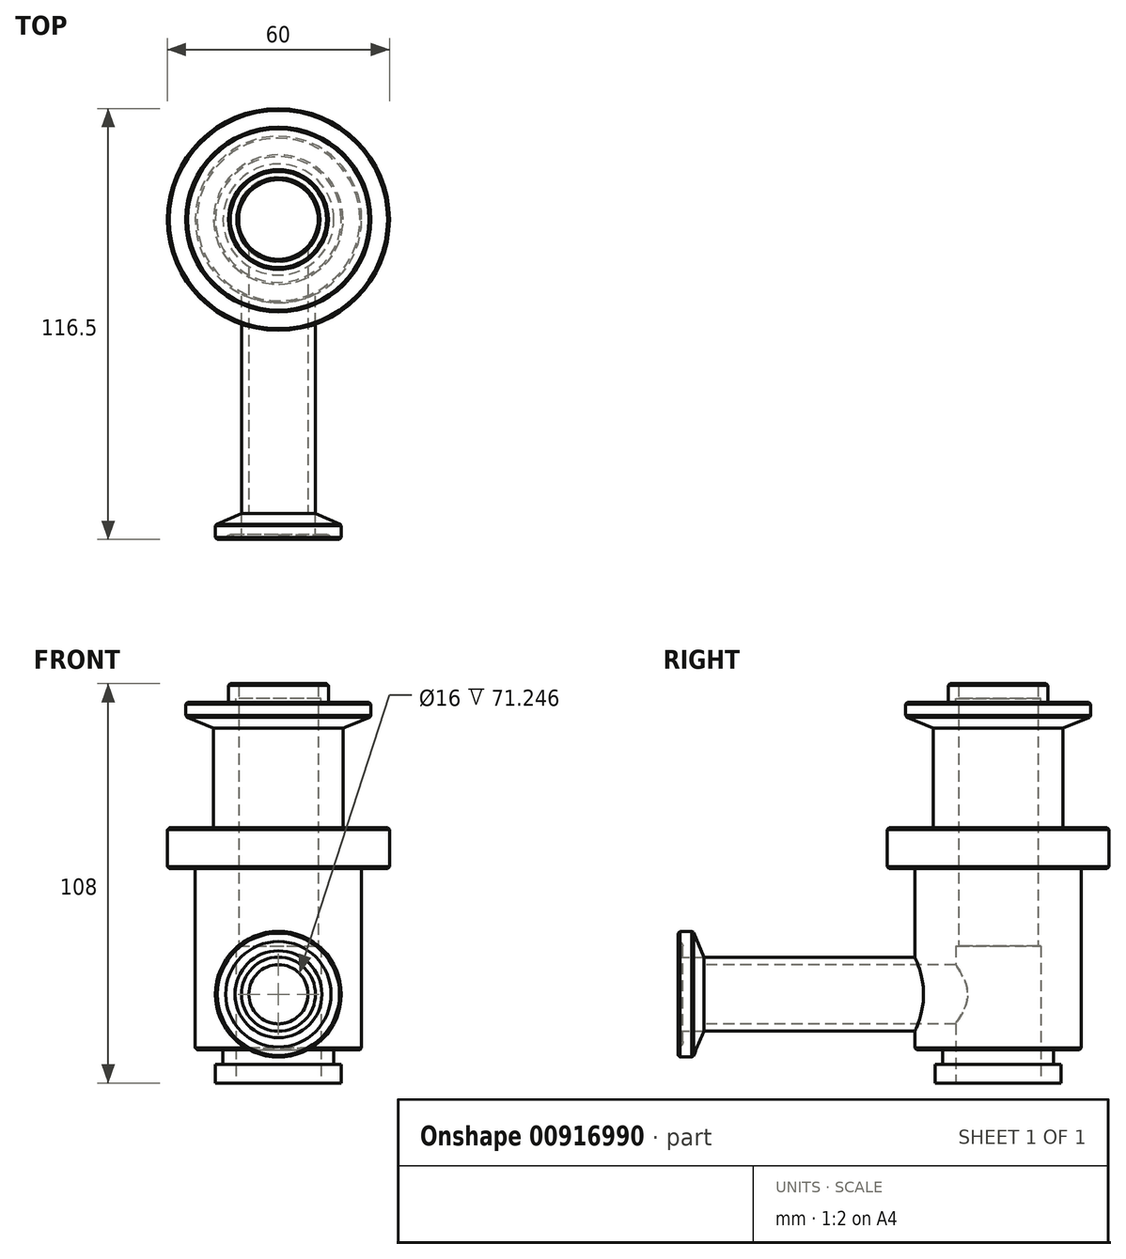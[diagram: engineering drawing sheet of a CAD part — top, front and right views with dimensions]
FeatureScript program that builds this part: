
annotation { "Feature Type Name" : "Feature", "Feature Type Description" : "" }
export const myFeature = defineFeature(function(context is Context, id is Id, definition is map)
    precondition{}
    {
        {
            var Q0;
            Q0=qCreatedBy(makeId("Top.planeOp"),FACE);
            var sketch = newSketch(context, id + "F0", { "sketchPlane" : qUnion([Q0])});
            skCircle(sketch, "E0", {"center": v(0, 0) * mm, "radius": 13.5 * mm});
            skCircle(sketch, "E1", {"center": v(0, 0) * mm, "radius": 10.75 * mm});
            skSolve(sketch);
        }
        {
            var Q0;
            Q0=makeQuery(id+"F0.imprint","IMPRINT",FACE,{"disambiguationData":[TD([[makeQuery(id+"F0.imprint","IMPRINT",EDGE,{"derivedFrom":sQuery(id+"F0.wireOp",EDGE,"E0")}),1.0]])]});
            extrude(context, id + "F1", {"entities" : qUnion([Q0]), "depth" : 5 * mm, "offsetDistance" : 25 * mm});
        }
        {
            var Q0;
            Q0=makeQuery(id+"F1.opExtrude","CAP_FACE",FACE,{"disambiguationData":[OSD([sQuery(id+"F0.wireOp",EDGE,"E0"),sQuery(id+"F0.wireOp",EDGE,"E1")])],"isStart":true});
            var sketch = newSketch(context, id + "F2", { "sketchPlane" : qUnion([Q0])});
            skCircle(sketch, "E2", {"center": v(0, 0) * mm, "radius": 25 * mm});
            skSolve(sketch);
        }
        {
            var Q0;
            Q0=makeQuery(id+"F2.imprint","IMPRINT",FACE,{"disambiguationData":[TD([[makeQuery(id+"F2.imprint","IMPRINT",EDGE,{"derivedFrom":makeQuery(id+"F1.opExtrude","CAP_EDGE",EDGE,{"disambiguationData":[OSD([sQuery(id+"F0.wireOp",EDGE,"E0")])],"isStart":true})}),-1.0]])]});
            var Q1;
            Q1=makeQuery(id+"F2.imprint","IMPRINT",FACE,{"disambiguationData":[TD([[makeQuery(id+"F2.imprint","IMPRINT",EDGE,{"derivedFrom":makeQuery(id+"F1.opExtrude","CAP_EDGE",EDGE,{"disambiguationData":[OSD([sQuery(id+"F0.wireOp",EDGE,"E1")])],"isStart":true})}),-1.0]])]});
            var Q2;
            Q2=makeQuery(id+"F2.imprint","IMPRINT",FACE,{"disambiguationData":[TD([[makeQuery(id+"F2.imprint","IMPRINT",EDGE,{"derivedFrom":sQuery(id+"F2.wireOp",EDGE,"E2")}),1.0]])]});
            extrude(context, id + "F3", {"entities" : qUnion([Q0, Q1, Q2]), "operationType" : NewBodyOperationType.ADD, "depth" : 7 * mm, "offsetDistance" : 25 * mm});
        }
        {
            var Q0;
            Q0=makeQuery(id+"F3.opExtrude","CAP_FACE",FACE,{"disambiguationData":[OSD([sQuery(id+"F2.wireOp",EDGE,"E2")])],"isStart":false});
            var sketch = newSketch(context, id + "F4", { "sketchPlane" : qUnion([Q0])});
            skCircle(sketch, "E3", {"center": v(0, 0) * mm, "radius": 17.5 * mm});
            skSolve(sketch);
        }
        {
            var Q0;
            Q0 = qSketchRegion(id + "F4", true);
            extrude(context, id + "F5", {"entities" : qUnion([Q0]), "operationType" : NewBodyOperationType.ADD, "depth" : 27 * mm, "offsetDistance" : 25 * mm});
        }
        {
            var Q0;
            Q0=makeQuery(id+"F5.opExtrude","CAP_FACE",FACE,{"disambiguationData":[OSD([sQuery(id+"F4.wireOp",EDGE,"E3")])],"isStart":false});
            var sketch = newSketch(context, id + "F6", { "sketchPlane" : qUnion([Q0])});
            skCircle(sketch, "E4", {"center": v(0, 0) * mm, "radius": 30 * mm});
            skSolve(sketch);
        }
        {
            var Q0;
            Q0=makeQuery(id+"F6.imprint","IMPRINT",FACE,{"disambiguationData":[TD([[makeQuery(id+"F6.imprint","IMPRINT",EDGE,{"derivedFrom":makeQuery(id+"F5.opExtrude","CAP_EDGE",EDGE,{"disambiguationData":[OSD([sQuery(id+"F4.wireOp",EDGE,"E3")])],"isStart":false})}),1.0]])]});
            var Q1;
            Q1=makeQuery(id+"F6.imprint","IMPRINT",FACE,{"disambiguationData":[TD([[makeQuery(id+"F6.imprint","IMPRINT",EDGE,{"derivedFrom":sQuery(id+"F6.wireOp",EDGE,"E4")}),1.0]])]});
            extrude(context, id + "F7", {"entities" : qUnion([Q0, Q1]), "operationType" : NewBodyOperationType.ADD, "depth" : 11 * mm, "offsetDistance" : 25 * mm});
        }
        {
            var Q0;
            Q0=makeQuery(id+"F7.opExtrude","CAP_FACE",FACE,{"disambiguationData":[OSD([sQuery(id+"F6.wireOp",EDGE,"E4")])],"isStart":false});
            var sketch = newSketch(context, id + "F8", { "sketchPlane" : qUnion([Q0])});
            skCircle(sketch, "E5", {"center": v(0, 0) * mm, "radius": 22.5 * mm});
            skSolve(sketch);
        }
        {
            var Q0;
            Q0=makeQuery(id+"F8.imprint","IMPRINT",FACE,{"disambiguationData":[TD([[makeQuery(id+"F8.imprint","IMPRINT",EDGE,{"derivedFrom":sQuery(id+"F8.wireOp",EDGE,"E5")}),1.0]])]});
            extrude(context, id + "F9", {"entities" : qUnion([Q0]), "operationType" : NewBodyOperationType.ADD, "depth" : 49 * mm, "offsetDistance" : 25 * mm});
        }
        {
            var Q0;
            Q0=makeQuery(id+"F9.opExtrude","CAP_FACE",FACE,{"disambiguationData":[OSD([sQuery(id+"F8.wireOp",EDGE,"E5")])],"isStart":false});
            var sketch = newSketch(context, id + "F10", { "sketchPlane" : qUnion([Q0])});
            skCircle(sketch, "E6", {"center": v(0, 0) * mm, "radius": 15 * mm});
            skSolve(sketch);
        }
        {
            var Q0;
            Q0=makeQuery(id+"F10.imprint","IMPRINT",FACE,{"disambiguationData":[TD([[makeQuery(id+"F10.imprint","IMPRINT",EDGE,{"derivedFrom":sQuery(id+"F10.wireOp",EDGE,"E6")}),1.0]])]});
            extrude(context, id + "F11", {"entities" : qUnion([Q0]), "operationType" : NewBodyOperationType.ADD, "depth" : 4 * mm, "offsetDistance" : 25 * mm});
        }
        {
            var Q0;
            Q0=makeQuery(id+"F11.opExtrude","CAP_FACE",FACE,{"disambiguationData":[OSD([sQuery(id+"F10.wireOp",EDGE,"E6")])],"isStart":false});
            var sketch = newSketch(context, id + "F12", { "sketchPlane" : qUnion([Q0])});
            skCircle(sketch, "E7", {"center": v(0, 0) * mm, "radius": 17 * mm});
            skSolve(sketch);
        }
        {
            var Q0;
            Q0=makeQuery(id+"F12.imprint","IMPRINT",FACE,{"disambiguationData":[TD([[makeQuery(id+"F12.imprint","IMPRINT",EDGE,{"derivedFrom":sQuery(id+"F12.wireOp",EDGE,"E7")}),1.0]])]});
            var Q1;
            Q1=makeQuery(id+"F12.imprint","IMPRINT",FACE,{"disambiguationData":[TD([[makeQuery(id+"F12.imprint","IMPRINT",EDGE,{"derivedFrom":makeQuery(id+"F11.opExtrude","CAP_EDGE",EDGE,{"disambiguationData":[OSD([sQuery(id+"F10.wireOp",EDGE,"E6")])],"isStart":false})}),1.0]])]});
            extrude(context, id + "F13", {"entities" : qUnion([Q0, Q1]), "operationType" : NewBodyOperationType.ADD, "depth" : 5 * mm, "offsetDistance" : 25 * mm});
        }
        {
            var Q0;
            Q0=makeQuery(id+"F13.opExtrude","CAP_FACE",FACE,{"disambiguationData":[OSD([sQuery(id+"F12.wireOp",EDGE,"E7")])],"isStart":false});
            var sketch = newSketch(context, id + "F14", { "sketchPlane" : qUnion([Q0])});
            skCircle(sketch, "E8", {"center": v(0, 0) * mm, "radius": 11.5 * mm});
            skSolve(sketch);
        }
        {
            var Q0;
            Q0=makeQuery(id+"F14.imprint","IMPRINT",FACE,{"disambiguationData":[TD([[makeQuery(id+"F14.imprint","IMPRINT",EDGE,{"derivedFrom":sQuery(id+"F14.wireOp",EDGE,"E8")}),1.0]])]});
            extrude(context, id + "F15", {"entities" : qUnion([Q0]), "operationType" : NewBodyOperationType.REMOVE, "oppositeDirection" : true, "depth" : 37 * mm, "offsetDistance" : 25 * mm});
        }
        {
            var Q0;
            Q0=makeQuery(id+"F3.boolean.opBoolean","SPLIT",FACE,{"disambiguationData":[TD([makeQuery(id+"F1.opExtrude","SWEPT_FACE",FACE,{"disambiguationData":[OSD([sQuery(id+"F0.wireOp",EDGE,"E1")])]})])],"derivedFrom":makeQuery(id+"F3.opExtrude","CAP_FACE",FACE,{"disambiguationData":[OSD([sQuery(id+"F2.wireOp",EDGE,"E2")])],"isStart":true})});
            var sketch = newSketch(context, id + "F16", { "sketchPlane" : qUnion([Q0])});
            skCircle(sketch, "E9", {"center": v(0, 0) * mm, "radius": 10.75 * mm});
            skSolve(sketch);
        }
        {
            var Q0;
            Q0=makeQuery(id+"F16.imprint","IMPRINT",FACE,{"disambiguationData":[TD([[makeQuery(id+"F16.imprint","IMPRINT",EDGE,{"derivedFrom":sQuery(id+"F16.wireOp",EDGE,"E9")}),1.0]])]});
            extrude(context, id + "F17", {"entities" : qUnion([Q0]), "operationType" : NewBodyOperationType.REMOVE, "endBound" : BoundingType.THROUGH_ALL, "oppositeDirection" : true, "depth" : 25 * mm, "offsetDistance" : 25 * mm});
        }
        {
            var Q0;
            Q0=makeQuery(id+"F15.boolean.opBoolean","COPY",EDGE,{"derivedFrom":makeQuery(id+"F15.opExtrude","CAP_EDGE",EDGE,{"disambiguationData":[OSD([sQuery(id+"F14.wireOp",EDGE,"E8")])],"isStart":true})});
            var Q1;
            Q1=makeQuery(id+"F9.opExtrude","CAP_EDGE",EDGE,{"disambiguationData":[OSD([sQuery(id+"F8.wireOp",EDGE,"E5")])],"isStart":false});
            var Q2;
            Q2=makeQuery(id+"F7.opExtrude","CAP_EDGE",EDGE,{"disambiguationData":[OSD([sQuery(id+"F6.wireOp",EDGE,"E4")])],"isStart":false});
            var Q3;
            Q3=makeQuery(id+"F7.opExtrude","CAP_EDGE",EDGE,{"disambiguationData":[OSD([sQuery(id+"F6.wireOp",EDGE,"E4")])],"isStart":true});
            var Q4;
            Q4=makeQuery(id+"F3.opExtrude","CAP_EDGE",EDGE,{"disambiguationData":[OSD([sQuery(id+"F2.wireOp",EDGE,"E2")])],"isStart":true});
            var Q5;
            Q5=makeQuery(id+"F1.opExtrude","CAP_EDGE",EDGE,{"disambiguationData":[OSD([sQuery(id+"F0.wireOp",EDGE,"E0")])],"isStart":false});
            var Q6;
            Q6=makeQuery(id+"F1.opExtrude","CAP_EDGE",EDGE,{"disambiguationData":[OSD([sQuery(id+"F0.wireOp",EDGE,"E1")])],"isStart":false});
            chamfer(context, id + "F18", {"entities" : qUnion([Q0, Q1, Q2, Q3, Q4, Q5, Q6]), "width" : .5 * mm, "tangentPropagation" : true});
        }
        {
            var Q0;
            Q0=makeQuery(id+"F3.opExtrude","CAP_EDGE",EDGE,{"disambiguationData":[OSD([sQuery(id+"F2.wireOp",EDGE,"E2")])],"isStart":false});
            chamfer(context, id + "F19", {"entities" : qUnion([Q0]), "chamferType" : ChamferType.TWO_OFFSETS, "width1" : 7.5 * mm, "oppositeDirection" : false, "width2" : 3 * mm, "tangentPropagation" : true});
        }
        {
            var Q0;
            {var subQ0=sQuery(id+"F2.wireOp",EDGE,"E2");Q0=makeQuery(id+"F19.opChamfer","BLEND_EDGE",EDGE,{"blendedFrom":[makeQuery(id+"F3.opExtrude","CAP_EDGE",EDGE,{"disambiguationData":[OSD([subQ0])],"isStart":false}),makeQuery(id+"F3.opExtrude","SWEPT_FACE",FACE,{"disambiguationData":[OSD([subQ0])]})],"blendedInto":[makeQuery(id+"F3.opExtrude","SWEPT_FACE",FACE,{"disambiguationData":[OSD([subQ0])]})]});}
            chamfer(context, id + "F20", {"entities" : qUnion([Q0]), "width" : .5 * mm, "tangentPropagation" : true});
        }
        {
            var Q0;
            Q0=qCreatedBy(makeId("Front.planeOp"),FACE);
            cPlane(context, id + "F21", {"entities" : qUnion([Q0]), "cplaneType" : CPlaneType.OFFSET, "offset" : 22.5 * mm, "width" : 150 * mm, "height" : 150 * mm});
        }
        {
            var Q0;
            Q0=qCreatedBy(id+"F21.planeOp",FACE);
            var sketch = newSketch(context, id + "F22", { "sketchPlane" : qUnion([Q0])});
            skCircle(sketch, "E10", {"center": v(0, -79) * mm, "radius": 10 * mm});
            skSolve(sketch);
        }
        {
            var Q0;
            Q0=makeQuery(id+"F22.imprint","IMPRINT",FACE,{"disambiguationData":[TD([[makeQuery(id+"F22.imprint","IMPRINT",EDGE,{"derivedFrom":sQuery(id+"F22.wireOp",EDGE,"E10")}),1.0]])]});
            extrude(context, id + "F23", {"entities" : qUnion([Q0]), "operationType" : NewBodyOperationType.ADD, "depth" : 57 * mm, "offsetDistance" : 25 * mm, "hasSecondDirection" : true, "secondDirectionBound" : BoundingType.UP_TO_NEXT, "secondDirectionOppositeDirection" : true, "secondDirectionDepth" : 25 * mm});
        }
        {
            var Q0;
            {var subQ0=sQuery(id+"F22.wireOp",EDGE,"E10");Q0=makeQuery(id+"F23.opExtrude","CAP_FACE",FACE,{"disambiguationData":[OSD([subQ0]),topologyDisambiguationEdgeConnected([makeQuery(id+"F22.imprint","IMPRINT",EDGE,{"derivedFrom":subQ0})])],"isStart":false});}
            var sketch = newSketch(context, id + "F24", { "sketchPlane" : qUnion([Q0])});
            skCircle(sketch, "E11", {"center": v(0, -79) * mm, "radius": 8 * mm});
            skSolve(sketch);
        }
        {
            var Q0;
            Q0=makeQuery(id+"F24.imprint","IMPRINT",FACE,{"disambiguationData":[TD([[makeQuery(id+"F24.imprint","IMPRINT",EDGE,{"derivedFrom":sQuery(id+"F24.wireOp",EDGE,"E11")}),1.0]])]});
            extrude(context, id + "F25", {"entities" : qUnion([Q0]), "operationType" : NewBodyOperationType.REMOVE, "endBound" : BoundingType.UP_TO_NEXT, "oppositeDirection" : true, "depth" : 25 * mm, "offsetDistance" : 25 * mm});
        }
        {
            var Q0;
            {var subQ0=sQuery(id+"F22.wireOp",EDGE,"E10");Q0=makeQuery(id+"F23.opExtrude","CAP_FACE",FACE,{"disambiguationData":[OSD([subQ0]),topologyDisambiguationEdgeConnected([makeQuery(id+"F22.imprint","IMPRINT",EDGE,{"derivedFrom":subQ0})])],"isStart":false});}
            var sketch = newSketch(context, id + "F26", { "sketchPlane" : qUnion([Q0])});
            skCircle(sketch, "E12", {"center": v(0, -79) * mm, "radius": 17 * mm});
            skSolve(sketch);
        }
        {
            var Q0;
            Q0=makeQuery(id+"F26.imprint","IMPRINT",FACE,{"disambiguationData":[TD([[makeQuery(id+"F26.imprint","IMPRINT",EDGE,{"derivedFrom":sQuery(id+"F26.wireOp",EDGE,"E12")}),1.0]])]});
            var Q1;
            Q1=makeQuery(id+"F26.imprint","IMPRINT",FACE,{"disambiguationData":[TD([[makeQuery(id+"F26.imprint","IMPRINT",EDGE,{"derivedFrom":makeQuery(id+"F25.boolean.opBoolean","COPY",EDGE,{"derivedFrom":makeQuery(id+"F25.opExtrude","CAP_EDGE",EDGE,{"disambiguationData":[OSD([sQuery(id+"F24.wireOp",EDGE,"E11")])],"isStart":true})})}),-1.0]])]});
            extrude(context, id + "F27", {"entities" : qUnion([Q0, Q1]), "operationType" : NewBodyOperationType.ADD, "depth" : 7 * mm, "offsetDistance" : 25 * mm});
        }
        {
            var Q0;
            Q0=makeQuery(id+"F27.opExtrude","CAP_EDGE",EDGE,{"disambiguationData":[OSD([sQuery(id+"F26.wireOp",EDGE,"E12")])],"isStart":true});
            chamfer(context, id + "F28", {"entities" : qUnion([Q0]), "chamferType" : ChamferType.TWO_OFFSETS, "width1" : 3 * mm, "oppositeDirection" : false, "width2" : 7 * mm, "tangentPropagation" : true});
        }
        {
            var Q0;
            Q0=makeQuery(id+"F27.opExtrude","CAP_EDGE",EDGE,{"disambiguationData":[OSD([sQuery(id+"F26.wireOp",EDGE,"E12")])],"isStart":false});
            var Q1;
            {var subQ0=sQuery(id+"F26.wireOp",EDGE,"E12");Q1=makeQuery(id+"F28.opChamfer","BLEND_EDGE",EDGE,{"blendedFrom":[makeQuery(id+"F27.opExtrude","CAP_EDGE",EDGE,{"disambiguationData":[OSD([subQ0])],"isStart":true}),makeQuery(id+"F27.opExtrude","SWEPT_FACE",FACE,{"disambiguationData":[OSD([subQ0])]})],"blendedInto":[makeQuery(id+"F27.opExtrude","SWEPT_FACE",FACE,{"disambiguationData":[OSD([subQ0])]})]});}
            chamfer(context, id + "F29", {"entities" : qUnion([Q0, Q1]), "width" : .5 * mm, "tangentPropagation" : true});
        }
        {
            var Q0;
            Q0=qCreatedBy(makeId("Right.planeOp"),FACE);
            var sketch = newSketch(context, id + "F30", { "sketchPlane" : qUnion([Q0])});
            skCircle(sketch, "E13", {"center": v(-86.5, -66) * mm, "radius": 1.25 * mm});
            skPoint(sketch, "E14", {"position": v(-86, -62) * mm});
            skLineSegment(sketch, "E15", {"start": v(-62.54, -79) * mm, "end": v(-70.79, -79) * mm, "construction": true});
            skSolve(sketch);
        }
        {
            var Q0;
            Q0=makeQuery(id+"F30.imprint","IMPRINT",FACE,{"disambiguationData":[TD([[makeQuery(id+"F30.imprint","IMPRINT",EDGE,{"derivedFrom":sQuery(id+"F30.wireOp",EDGE,"E13")}),1.0]])]});
            var Q1;
            Q1=sQuery(id+"F30.wireOp",EDGE,"E15");
            revolve(context, id + "F31", {"operationType" : NewBodyOperationType.REMOVE, "surfaceOperationType" : NewSurfaceOperationType.NEW, "entities" : qUnion([Q0]), "axis" : qUnion([Q1]), "revolveType" : RevolveType.FULL, "oppositeDirection" : true});
        }
        {
            var Q0;
            Q0=makeQuery(id+"F1.opExtrude","CAP_FACE",FACE,{"disambiguationData":[OSD([sQuery(id+"F0.wireOp",EDGE,"E0"),sQuery(id+"F0.wireOp",EDGE,"E1")])],"isStart":false});
            cPlane(context, id + "F32", {"entities" : qUnion([Q0]), "cplaneType" : CPlaneType.OFFSET, "offset" : 4 * mm, "oppositeDirection" : true, "width" : 150 * mm, "height" : 150 * mm});
        }
        {
            var Q0;
            Q0=qCreatedBy(id+"F32.planeOp",FACE);
            var sketch = newSketch(context, id + "F33", { "sketchPlane" : qUnion([Q0])});
            skCircle(sketch, "E16", {"center": v(0, 0) * mm, "radius": 11.5 * mm});
            skSolve(sketch);
        }
        {
            var Q0;
            Q0=makeQuery(id+"F33.imprint","IMPRINT",FACE,{"disambiguationData":[TD([[makeQuery(id+"F33.imprint","IMPRINT",EDGE,{"derivedFrom":sQuery(id+"F33.wireOp",EDGE,"E16")}),1.0]])]});
            extrude(context, id + "F34", {"entities" : qUnion([Q0]), "operationType" : NewBodyOperationType.REMOVE, "oppositeDirection" : true, "depth" : 1.1 * mm, "offsetDistance" : 25 * mm});
        }
    });
